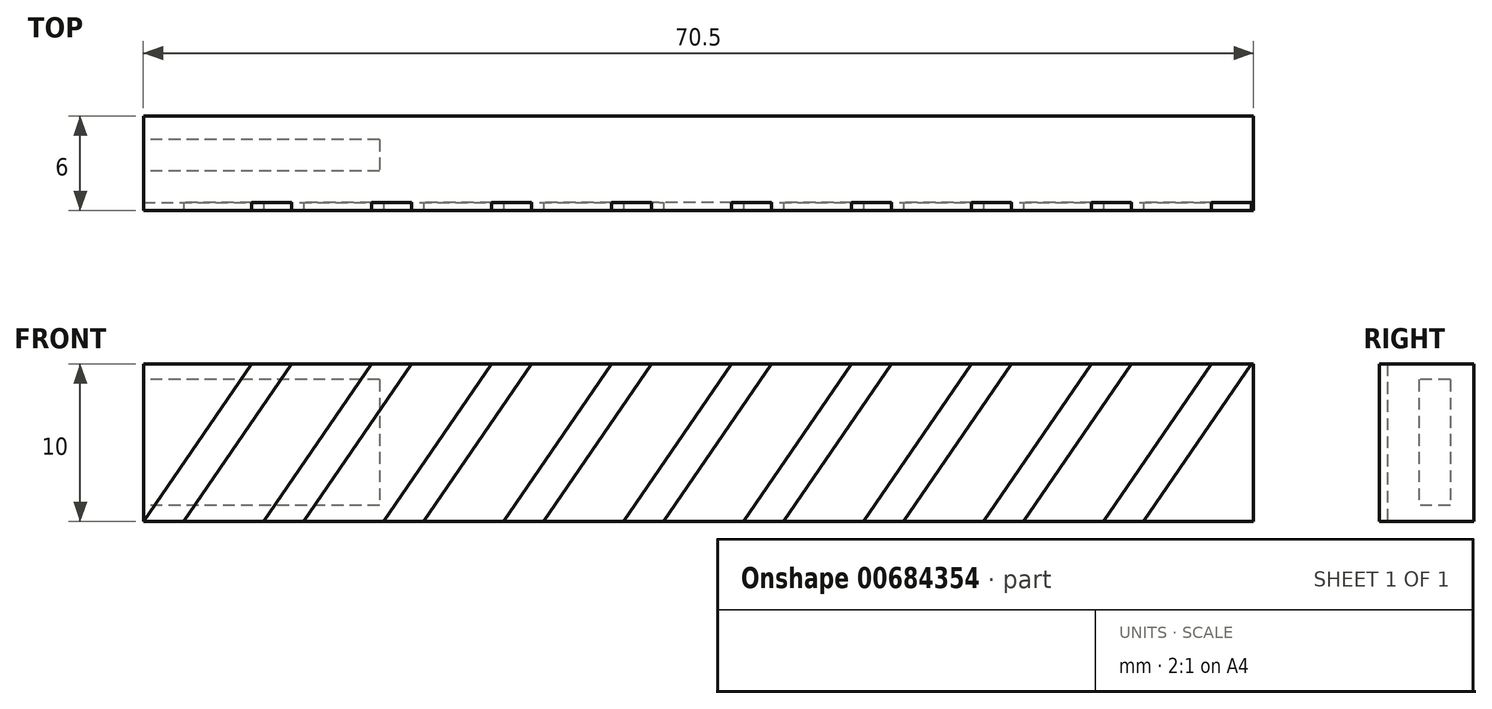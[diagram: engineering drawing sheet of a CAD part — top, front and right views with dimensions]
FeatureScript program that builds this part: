
annotation { "Feature Type Name" : "Feature", "Feature Type Description" : "" }
export const myFeature = defineFeature(function(context is Context, id is Id, definition is map)
    precondition{}
    {
        {
            var Q0;
            Q0=qCreatedBy(makeId("Front.planeOp"),FACE);
            var sketch = newSketch(context, id + "F0", { "sketchPlane" : qUnion([Q0])});
            skLineSegment(sketch, "E0.bottom", {"start": v(-12.6, 46.13) * mm, "end": v(57.9, 46.13) * mm});
            skLineSegment(sketch, "E0.top", {"start": v(-12.6, 36.13) * mm, "end": v(57.9, 36.13) * mm});
            skLineSegment(sketch, "E0.left", {"start": v(-12.6, 46.13) * mm, "end": v(-12.6, 36.13) * mm});
            skLineSegment(sketch, "E0.right", {"start": v(57.9, 46.13) * mm, "end": v(57.9, 36.13) * mm});
            skSolve(sketch);
        }
        {
            var Q0;
            Q0=makeQuery(id+"F0.imprint","IMPRINT",FACE,{"disambiguationData":[TD([[makeQuery(id+"F0.imprint","IMPRINT",EDGE,{"derivedFrom":sQuery(id+"F0.wireOp",EDGE,"E0.bottom")}),-1.0]])]});
            extrude(context, id + "F1", {"entities" : qUnion([Q0]), "depth" : 6 * mm, "offsetDistance" : 25.4 * mm});
        }
        {
            var Q0;
            Q0=makeQuery(id+"F1.opExtrude","CAP_FACE",FACE,{"disambiguationData":[OSD([sQuery(id+"F0.wireOp",EDGE,"E0.bottom"),sQuery(id+"F0.wireOp",EDGE,"E0.top"),sQuery(id+"F0.wireOp",EDGE,"E0.left"),sQuery(id+"F0.wireOp",EDGE,"E0.right")])],"isStart":false});
            var sketch = newSketch(context, id + "F2", { "sketchPlane" : qUnion([Q0])});
            skLineSegment(sketch, "E1", {"start": v(-12.6, 36.13) * mm, "end": v(-5.73, 46.13) * mm});
            skLineSegment(sketch, "E2", {"start": v(-5.73, 46.13) * mm, "end": v(-3.19, 46.13) * mm});
            skLineSegment(sketch, "E3", {"start": v(-3.19, 46.13) * mm, "end": v(-10.07, 36.13) * mm});
            skLineSegment(sketch, "E4", {"start": v(-10.07, 36.13) * mm, "end": v(-12.6, 36.13) * mm});
            skLineSegment(sketch, "E5", {"start": v(1.9, 46.13) * mm, "end": v(4.43, 46.13) * mm});
            skLineSegment(sketch, "E6", {"start": v(4.43, 46.13) * mm, "end": v(-2.45, 36.13) * mm});
            skLineSegment(sketch, "E7", {"start": v(-2.45, 36.13) * mm, "end": v(-4.99, 36.13) * mm});
            skLineSegment(sketch, "E8", {"start": v(-4.99, 36.13) * mm, "end": v(1.9, 46.13) * mm});
            skLineSegment(sketch, "E9", {"start": v(9.51, 46.13) * mm, "end": v(12.05, 46.13) * mm});
            skLineSegment(sketch, "E10", {"start": v(12.05, 46.13) * mm, "end": v(5.17, 36.13) * mm});
            skLineSegment(sketch, "E11", {"start": v(5.17, 36.13) * mm, "end": v(2.63, 36.13) * mm});
            skLineSegment(sketch, "E12", {"start": v(2.63, 36.13) * mm, "end": v(9.51, 46.13) * mm});
            skLineSegment(sketch, "E13", {"start": v(17.13, 46.13) * mm, "end": v(19.67, 46.13) * mm});
            skLineSegment(sketch, "E14", {"start": v(19.67, 46.13) * mm, "end": v(12.8, 36.13) * mm});
            skLineSegment(sketch, "E15", {"start": v(12.8, 36.13) * mm, "end": v(10.25, 36.13) * mm});
            skLineSegment(sketch, "E16", {"start": v(10.25, 36.13) * mm, "end": v(17.13, 46.13) * mm});
            skLineSegment(sketch, "E17", {"start": v(24.75, 46.13) * mm, "end": v(27.3, 46.13) * mm});
            skLineSegment(sketch, "E18", {"start": v(27.3, 46.13) * mm, "end": v(20.41, 36.13) * mm});
            skLineSegment(sketch, "E19", {"start": v(32.37, 46.13) * mm, "end": v(34.91, 46.13) * mm});
            skLineSegment(sketch, "E20", {"start": v(34.91, 46.13) * mm, "end": v(28.03, 36.13) * mm});
            skLineSegment(sketch, "E21", {"start": v(28.03, 36.13) * mm, "end": v(25.5, 36.13) * mm});
            skLineSegment(sketch, "E22", {"start": v(25.5, 36.13) * mm, "end": v(32.37, 46.13) * mm});
            skLineSegment(sketch, "E23", {"start": v(40, 46.13) * mm, "end": v(42.53, 46.13) * mm});
            skLineSegment(sketch, "E24", {"start": v(42.53, 46.13) * mm, "end": v(35.65, 36.13) * mm});
            skLineSegment(sketch, "E25", {"start": v(35.65, 36.13) * mm, "end": v(33.11, 36.13) * mm});
            skLineSegment(sketch, "E26", {"start": v(33.11, 36.13) * mm, "end": v(40, 46.13) * mm});
            skLineSegment(sketch, "E27", {"start": v(24.75, 46.13) * mm, "end": v(17.87, 36.13) * mm});
            skLineSegment(sketch, "E28", {"start": v(17.87, 36.13) * mm, "end": v(20.41, 36.13) * mm});
            skLineSegment(sketch, "E29", {"start": v(47.61, 46.13) * mm, "end": v(50.15, 46.13) * mm});
            skLineSegment(sketch, "E30", {"start": v(50.15, 46.13) * mm, "end": v(43.27, 36.13) * mm});
            skLineSegment(sketch, "E31", {"start": v(43.27, 36.13) * mm, "end": v(40.73, 36.13) * mm});
            skLineSegment(sketch, "E32", {"start": v(40.73, 36.13) * mm, "end": v(47.61, 46.13) * mm});
            skLineSegment(sketch, "E33", {"start": v(55.23, 46.13) * mm, "end": v(57.77, 46.13) * mm});
            skLineSegment(sketch, "E34", {"start": v(57.77, 46.13) * mm, "end": v(50.9, 36.13) * mm});
            skLineSegment(sketch, "E35", {"start": v(50.9, 36.13) * mm, "end": v(48.35, 36.13) * mm});
            skLineSegment(sketch, "E36", {"start": v(48.35, 36.13) * mm, "end": v(55.23, 46.13) * mm});
            skSolve(sketch);
        }
        {
            var Q0;
            Q0 = qSketchRegion(id + "F2", true);
            extrude(context, id + "F3", {"entities" : qUnion([Q0]), "operationType" : NewBodyOperationType.REMOVE, "oppositeDirection" : true, "depth" : 0.5 * mm, "offsetDistance" : 25.4 * mm});
        }
        {
            var Q0;
            Q0=makeQuery(id+"F1.opExtrude","SWEPT_FACE",FACE,{"disambiguationData":[OSD([sQuery(id+"F0.wireOp",EDGE,"E0.left")])]});
            var sketch = newSketch(context, id + "F4", { "sketchPlane" : qUnion([Q0])});
            skLineSegment(sketch, "E37.bottom", {"start": v(1.5, 45.13) * mm, "end": v(3.5, 45.13) * mm});
            skLineSegment(sketch, "E37.top", {"start": v(1.5, 37.13) * mm, "end": v(3.5, 37.13) * mm});
            skLineSegment(sketch, "E37.left", {"start": v(1.5, 45.13) * mm, "end": v(1.5, 37.13) * mm});
            skLineSegment(sketch, "E37.right", {"start": v(3.5, 45.13) * mm, "end": v(3.5, 37.13) * mm});
            skSolve(sketch);
        }
        {
            var Q0;
            Q0 = qSketchRegion(id + "F4", true);
            extrude(context, id + "F5", {"entities" : qUnion([Q0]), "operationType" : NewBodyOperationType.REMOVE, "oppositeDirection" : true, "depth" : 15 * mm, "offsetDistance" : 25.4 * mm});
        }
    });
